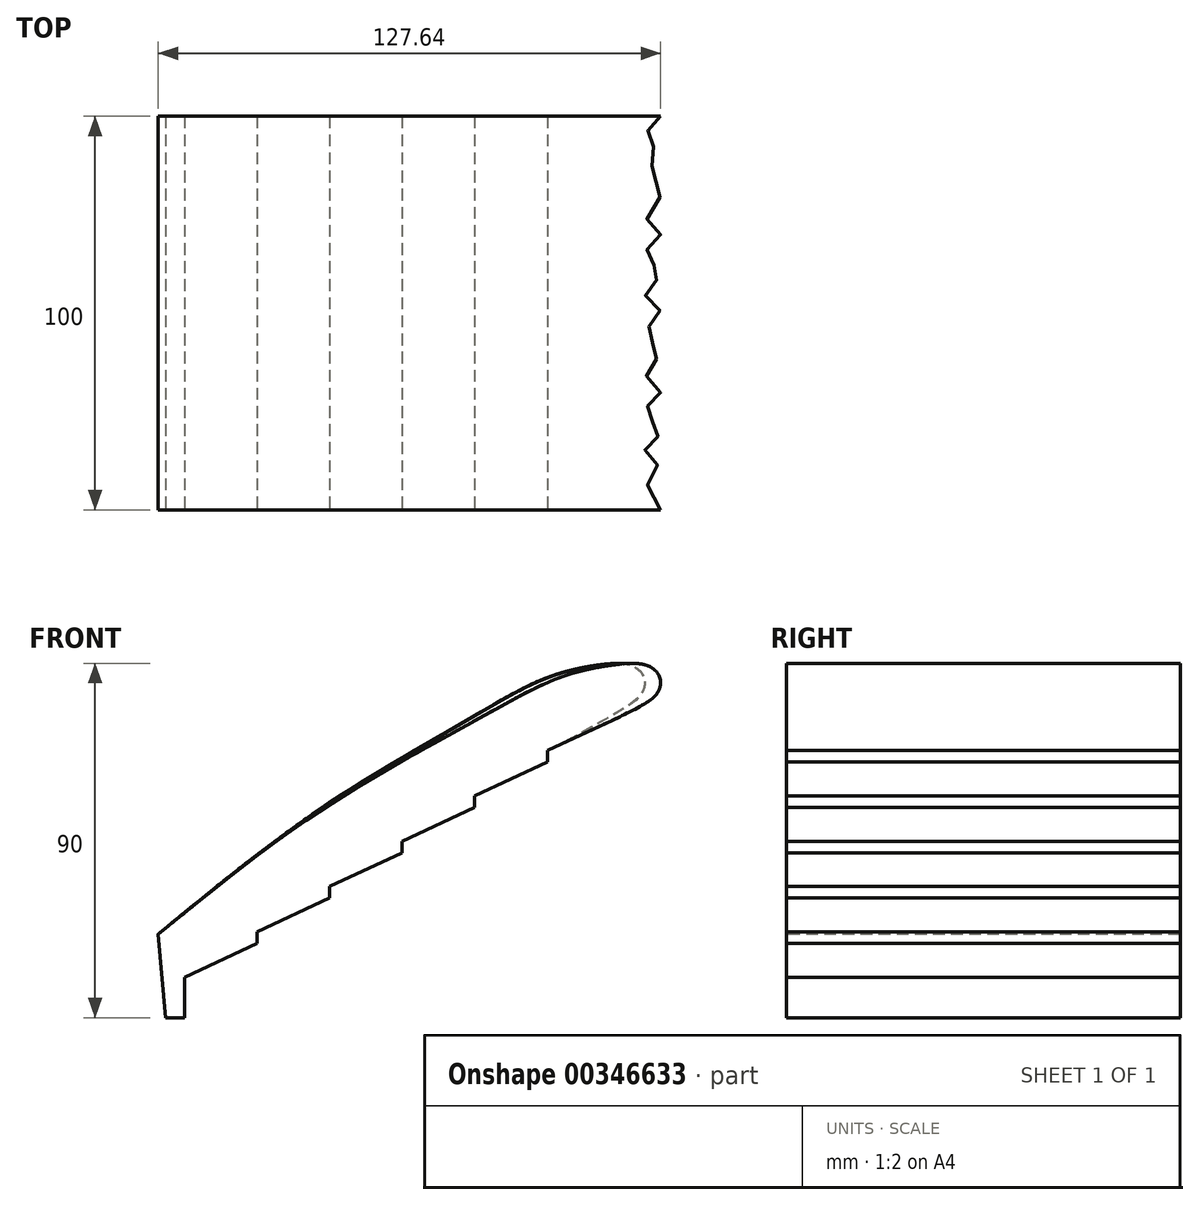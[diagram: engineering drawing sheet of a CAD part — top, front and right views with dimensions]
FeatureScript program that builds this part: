
annotation { "Feature Type Name" : "Feature", "Feature Type Description" : "" }
export const myFeature = defineFeature(function(context is Context, id is Id, definition is map)
    precondition{}
    {
        {
            var Q0;
            Q0=qCreatedBy(makeId("Front.planeOp"),FACE);
            var sketch = newSketch(context, id + "F0", { "sketchPlane" : qUnion([Q0])});
            skLineSegment(sketch, "E0", {"start": v(-10.35, -8.53) * mm, "end": v(-120.95, -77.64) * mm, "construction": true});
            skLineSegment(sketch, "E1", {"start": v(-10.35, -8.53) * mm, "end": v(-28.78, -17.12) * mm});
            skLineSegment(sketch, "E2", {"start": v(-28.78, -17.12) * mm, "end": v(-28.78, -20.05) * mm});
            skLineSegment(sketch, "E3", {"start": v(-28.78, -20.05) * mm, "end": v(-47.22, -28.64) * mm});
            skLineSegment(sketch, "E4", {"start": v(-47.22, -28.64) * mm, "end": v(-47.22, -31.57) * mm});
            skLineSegment(sketch, "E5", {"start": v(-47.22, -31.57) * mm, "end": v(-65.65, -40.16) * mm});
            skLineSegment(sketch, "E6", {"start": v(-65.65, -40.16) * mm, "end": v(-65.65, -43.08) * mm});
            skLineSegment(sketch, "E7", {"start": v(-65.65, -43.08) * mm, "end": v(-84.08, -51.68) * mm});
            skLineSegment(sketch, "E8", {"start": v(-84.08, -51.68) * mm, "end": v(-84.08, -54.6) * mm});
            skLineSegment(sketch, "E9", {"start": v(-84.08, -54.6) * mm, "end": v(-102.52, -63.2) * mm});
            skLineSegment(sketch, "E10", {"start": v(-102.52, -63.2) * mm, "end": v(-102.52, -66.12) * mm});
            skLineSegment(sketch, "E11", {"start": v(-102.52, -66.12) * mm, "end": v(-120.95, -74.72) * mm});
            skLineSegment(sketch, "E12", {"start": v(-120.95, -74.72) * mm, "end": v(-120.95, -77.64) * mm});
            skFitSpline(sketch, "E13", {"points": [v(-10.35, -8.53) * mm, v(-4.85, -5.69) * mm, v(-1.45, -3.27) * mm, v(-0.03, -0.46) * mm, v(-0.9, 2.72) * mm, v(-3.8, 4.6) * mm, v(-8.4, 4.97) * mm, v(-16.2, 3.96) * mm, v(-27.41, 0.72) * mm, v(-49.14, -10.61) * mm, v(-87.26, -32.96) * mm, v(-127.64, -63.77) * mm], "startDerivative": vector(74.5, 34.74) * mm, "endDerivative": vector(-206.83, -168.52) * mm});
            skLineSegment(sketch, "E14", {"start": v(-120.95, -77.64) * mm, "end": v(-120.95, -84.99) * mm});
            skLineSegment(sketch, "E15", {"start": v(-120.95, -84.99) * mm, "end": v(-125.77, -84.99) * mm});
            skLineSegment(sketch, "E16", {"start": v(-125.77, -84.99) * mm, "end": v(-127.64, -63.77) * mm});
            skPoint(sketch, "E17", {"position": v(-7.07, 5.01) * mm});
            skLineSegment(sketch, "E18", {"start": v(-7.07, 5.01) * mm, "end": v(1.85, 5.01) * mm, "construction": true});
            skPoint(sketch, "E19", {"position": v(0, 0) * mm});
            skLineSegment(sketch, "E20", {"start": v(0, 0) * mm, "end": v(0, 5.01) * mm, "construction": true});
            skSolve(sketch);
        }
        {
            var Q0;
            Q0=qCreatedBy(makeId("Top.planeOp"),FACE);
            var sketch = newSketch(context, id + "F1", { "sketchPlane" : qUnion([Q0])});
            skPoint(sketch, "E21", {"position": v(0, -100) * mm});
            skPoint(sketch, "E22", {"position": v(0, -10) * mm});
            skPoint(sketch, "E23", {"position": v(0, -20) * mm});
            skPoint(sketch, "E24", {"position": v(0, -30) * mm});
            skPoint(sketch, "E25", {"position": v(0, -40) * mm});
            skPoint(sketch, "E26", {"position": v(0, -50) * mm});
            skPoint(sketch, "E27", {"position": v(0, -60) * mm});
            skPoint(sketch, "E28", {"position": v(0, -70) * mm});
            skPoint(sketch, "E29", {"position": v(0, -80) * mm});
            skPoint(sketch, "E30", {"position": v(0, -90) * mm});
            skLineSegment(sketch, "E31", {"start": v(0, 0) * mm, "end": v(0, -10) * mm, "construction": true});
            skLineSegment(sketch, "E32", {"start": v(0, -10) * mm, "end": v(0, -20) * mm, "construction": true});
            skLineSegment(sketch, "E33", {"start": v(0, -20) * mm, "end": v(0, -30) * mm, "construction": true});
            skLineSegment(sketch, "E34", {"start": v(0, -30) * mm, "end": v(0, -40) * mm, "construction": true});
            skLineSegment(sketch, "E35", {"start": v(0, -40) * mm, "end": v(0, -50) * mm, "construction": true});
            skLineSegment(sketch, "E36", {"start": v(0, -50) * mm, "end": v(0, -60) * mm, "construction": true});
            skLineSegment(sketch, "E37", {"start": v(0, -60) * mm, "end": v(0, -70) * mm, "construction": true});
            skLineSegment(sketch, "E38", {"start": v(0, -70) * mm, "end": v(0, -80) * mm, "construction": true});
            skLineSegment(sketch, "E39", {"start": v(0, -80) * mm, "end": v(0, -90) * mm, "construction": true});
            skLineSegment(sketch, "E40", {"start": v(0, -90) * mm, "end": v(0, -100) * mm, "construction": true});
            skPoint(sketch, "E41", {"position": v(-4, -5) * mm});
            skPoint(sketch, "E41.positionSnap0", {"position": v(0, -5) * mm});
            skPoint(sketch, "E42", {"position": v(-4, -15) * mm});
            skPoint(sketch, "E42.positionSnap0", {"position": v(0, -15) * mm});
            skPoint(sketch, "E43", {"position": v(-4, -25) * mm});
            skPoint(sketch, "E43.positionSnap0", {"position": v(0, -25) * mm});
            skPoint(sketch, "E44", {"position": v(-4, -35) * mm});
            skPoint(sketch, "E44.positionSnap0", {"position": v(0, -35) * mm});
            skPoint(sketch, "E45", {"position": v(-4, -45) * mm});
            skPoint(sketch, "E45.positionSnap0", {"position": v(0, -45) * mm});
            skPoint(sketch, "E46", {"position": v(-4, -55) * mm});
            skPoint(sketch, "E46.positionSnap0", {"position": v(0, -55) * mm});
            skPoint(sketch, "E47", {"position": v(-4, -65) * mm});
            skPoint(sketch, "E47.positionSnap0", {"position": v(0, -65) * mm});
            skPoint(sketch, "E48", {"position": v(-4, -75) * mm});
            skPoint(sketch, "E48.positionSnap0", {"position": v(0, -75) * mm});
            skPoint(sketch, "E49", {"position": v(-4, -85) * mm});
            skPoint(sketch, "E49.positionSnap0", {"position": v(0, -85) * mm});
            skPoint(sketch, "E50", {"position": v(-4, -95) * mm});
            skPoint(sketch, "E50.positionSnap0", {"position": v(0, -95) * mm});
            skFitSpline(sketch, "E51", {"points": [v(0, 0) * mm, v(-4, -5) * mm, v(0, -10) * mm, v(-4, -15) * mm, v(0, -20) * mm, v(-4, -25) * mm, v(0, -30) * mm, v(-4, -35) * mm, v(0, -40) * mm, v(-4, -45) * mm, v(0, -50) * mm, v(-4, -55) * mm, v(0, -60) * mm, v(-4, -65) * mm, v(0, -70) * mm, v(-4, -75) * mm, v(0, -80) * mm, v(-4, -85) * mm, v(0, -90) * mm, v(-4, -95) * mm, v(0, -100) * mm], "startDerivative": vector(0, -100) * mm, "endDerivative": vector(0, -100) * mm});
            skPoint(sketch, "E52", {"position": v(-2, -97.5) * mm});
            skPoint(sketch, "E53", {"position": v(-2, -92.5) * mm});
            skPoint(sketch, "E54", {"position": v(-2, -87.5) * mm});
            skPoint(sketch, "E55", {"position": v(-2, -82.5) * mm});
            skPoint(sketch, "E56", {"position": v(-2, -77.5) * mm});
            skPoint(sketch, "E57", {"position": v(-2, -72.5) * mm});
            skPoint(sketch, "E58", {"position": v(-2, -67.5) * mm});
            skPoint(sketch, "E59", {"position": v(-2, -62.5) * mm});
            skPoint(sketch, "E60", {"position": v(-2, -57.5) * mm});
            skPoint(sketch, "E61", {"position": v(-2, -52.5) * mm});
            skPoint(sketch, "E62", {"position": v(-2, -47.5) * mm});
            skPoint(sketch, "E63", {"position": v(-2, -42.5) * mm});
            skPoint(sketch, "E64", {"position": v(-2, -37.5) * mm});
            skPoint(sketch, "E65", {"position": v(-2, -32.5) * mm});
            skPoint(sketch, "E66", {"position": v(-2, -27.5) * mm});
            skPoint(sketch, "E67", {"position": v(-2, -22.5) * mm});
            skPoint(sketch, "E68", {"position": v(-2, -17.5) * mm});
            skPoint(sketch, "E69", {"position": v(-2, -12.5) * mm});
            skPoint(sketch, "E70", {"position": v(-2, -7.5) * mm});
            skPoint(sketch, "E71", {"position": v(-2, -2.5) * mm});
            skSolve(sketch);
        }
        {
            var Q0;
            Q0=qCreatedBy(makeId("Front.planeOp"),FACE);
            cPlane(context, id + "F2", {"entities" : qUnion([Q0]), "cplaneType" : CPlaneType.OFFSET, "offset" : 100 * mm, "width" : 150 * mm, "height" : 150 * mm});
        }
        {
            var Q0;
            Q0=qCreatedBy(id+"F2.planeOp",FACE);
            var sketch = newSketch(context, id + "F3", { "sketchPlane" : qUnion([Q0])});
            skLineSegment(sketch, "E72", {"start": v(-10.35, -8.53) * mm, "end": v(-120.95, -77.64) * mm, "construction": true});
            skLineSegment(sketch, "E73", {"start": v(-10.35, -8.53) * mm, "end": v(-28.78, -17.12) * mm});
            skLineSegment(sketch, "E74", {"start": v(-28.78, -17.12) * mm, "end": v(-28.78, -20.05) * mm});
            skLineSegment(sketch, "E75", {"start": v(-28.78, -20.05) * mm, "end": v(-47.22, -28.64) * mm});
            skLineSegment(sketch, "E76", {"start": v(-47.22, -28.64) * mm, "end": v(-47.22, -31.57) * mm});
            skLineSegment(sketch, "E77", {"start": v(-47.22, -31.57) * mm, "end": v(-65.65, -40.16) * mm});
            skLineSegment(sketch, "E78", {"start": v(-65.65, -40.16) * mm, "end": v(-65.65, -43.08) * mm});
            skLineSegment(sketch, "E79", {"start": v(-65.65, -43.08) * mm, "end": v(-84.08, -51.68) * mm});
            skLineSegment(sketch, "E80", {"start": v(-84.08, -51.68) * mm, "end": v(-84.08, -54.6) * mm});
            skLineSegment(sketch, "E81", {"start": v(-84.08, -54.6) * mm, "end": v(-102.52, -63.2) * mm});
            skLineSegment(sketch, "E82", {"start": v(-102.52, -63.2) * mm, "end": v(-102.52, -66.12) * mm});
            skLineSegment(sketch, "E83", {"start": v(-102.52, -66.12) * mm, "end": v(-120.95, -74.72) * mm});
            skLineSegment(sketch, "E84", {"start": v(-120.95, -74.72) * mm, "end": v(-120.95, -77.64) * mm});
            skFitSpline(sketch, "E85", {"points": [v(-10.35, -8.53) * mm, v(-4.85, -5.69) * mm, v(-1.45, -3.27) * mm, v(-0.03, -0.46) * mm, v(-0.9, 2.72) * mm, v(-3.8, 4.6) * mm, v(-8.4, 4.97) * mm, v(-16.2, 3.96) * mm, v(-27.41, 0.72) * mm, v(-49.14, -10.61) * mm, v(-87.26, -32.96) * mm, v(-127.64, -63.77) * mm], "startDerivative": vector(74.5, 34.74) * mm, "endDerivative": vector(-206.83, -168.52) * mm});
            skLineSegment(sketch, "E86", {"start": v(-120.95, -77.64) * mm, "end": v(-120.95, -84.99) * mm});
            skLineSegment(sketch, "E87", {"start": v(-120.95, -84.99) * mm, "end": v(-125.77, -84.99) * mm});
            skLineSegment(sketch, "E88", {"start": v(-125.77, -84.99) * mm, "end": v(-127.64, -63.77) * mm});
            skPoint(sketch, "E89", {"position": v(-7.07, 5.01) * mm});
            skLineSegment(sketch, "E90", {"start": v(-7.07, 5.01) * mm, "end": v(1.85, 5.01) * mm, "construction": true});
            skPoint(sketch, "E91", {"position": v(0, 0) * mm});
            skLineSegment(sketch, "E92", {"start": v(0, 0) * mm, "end": v(0, 5.01) * mm, "construction": true});
            skSolve(sketch);
        }
        {
            var Q0;
            Q0=sQuery(id+"F1.wireOp",EDGE,"E51");
            var Q1;
            Q1=makeQuery(id+"F0.imprint","IMPRINT",FACE,{"disambiguationData":[TD([[makeQuery(id+"F0.imprint","IMPRINT",EDGE,{"derivedFrom":sQuery(id+"F0.wireOp",EDGE,"E1")}),-1.0]])]});
            var Q2;
            Q2=makeQuery(id+"F3.imprint","IMPRINT",FACE,{"disambiguationData":[TD([[makeQuery(id+"F3.imprint","IMPRINT",EDGE,{"derivedFrom":sQuery(id+"F3.wireOp",EDGE,"E73")}),-1.0]])]});
            var Q3;
            Q3=sQuery(id+"F1.wireOp",EDGE,"E51");
            var Q4;
            Q4=sQuery(id+"F0.wireOp",VERTEX,"E13.end");
            var Q5;
            Q5=sQuery(id+"F3.wireOp",VERTEX,"E85.end");
            loft(context, id + "F4", {"spine" : qUnion([Q0]), "addGuides" : true, "sheetProfilesArray" : [{ "sheetProfileEntities" : qUnion([Q1]) }, { "sheetProfileEntities" : qUnion([Q2]) }], "guidesArray" : [{ "guideEntities" : qUnion([Q3]), "guideDerivativeType" : LoftGuideDerivativeType.DEFAULT, "guideDerivativeMagnitude" : 1 }], "matchConnections" : true, "connections" : [{ "connectionEntities" : qUnion([Q4, Q5]), "connectionEdgeQueries" : qUnion([]), "connectionEdgeParameters" : [] }]});
        }
    });
